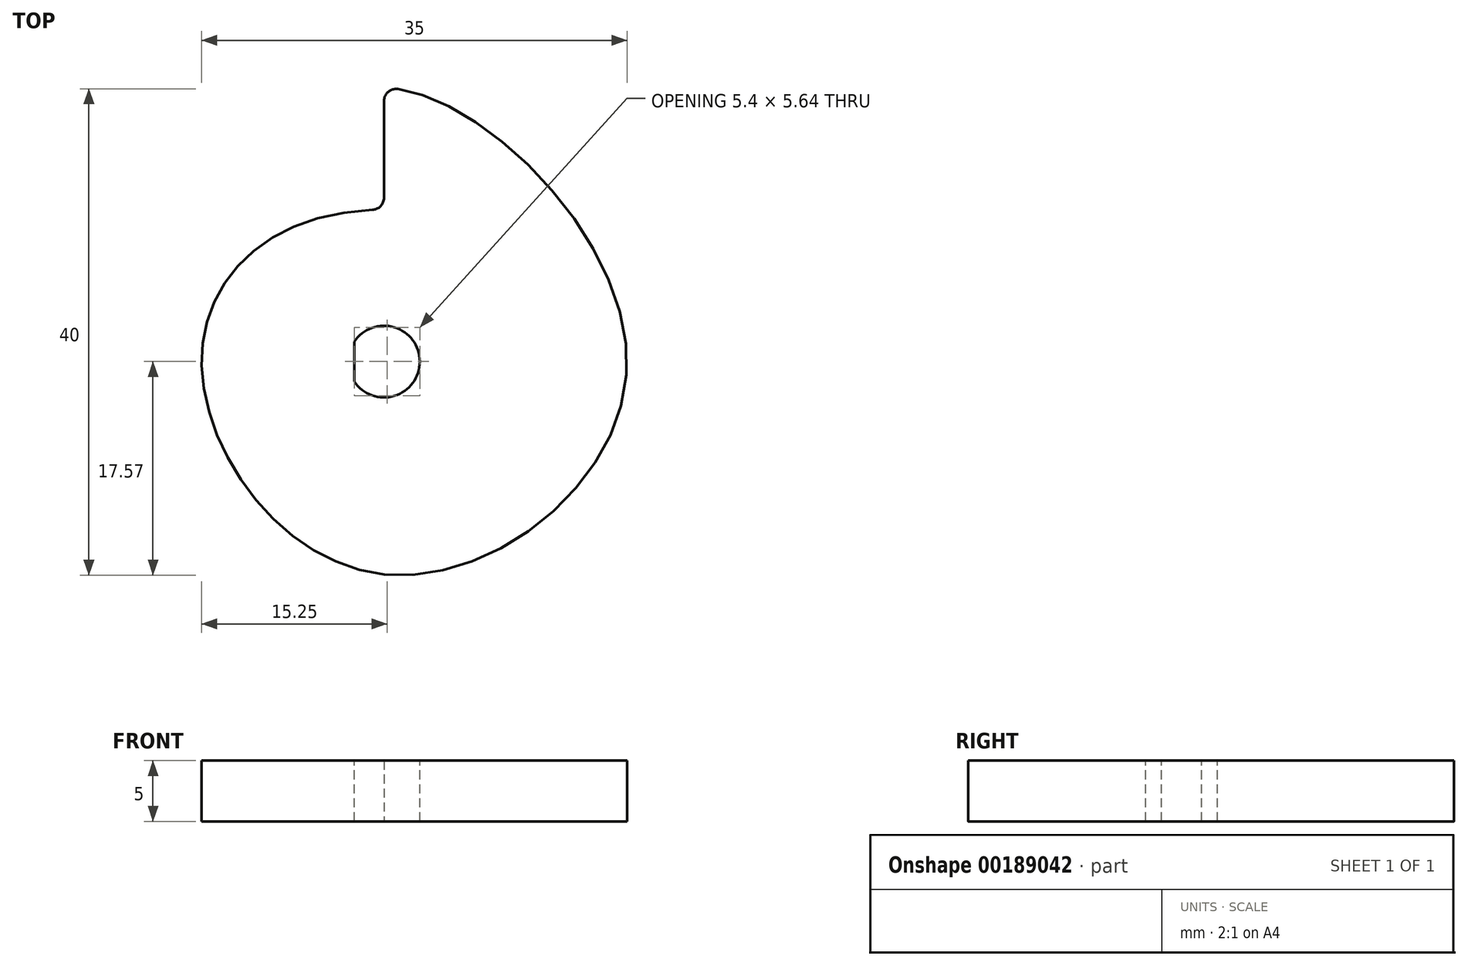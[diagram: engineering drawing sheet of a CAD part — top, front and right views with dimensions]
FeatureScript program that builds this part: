
annotation { "Feature Type Name" : "Feature", "Feature Type Description" : "" }
export const myFeature = defineFeature(function(context is Context, id is Id, definition is map)
    precondition{}
    {
        {
            var Q0;
            Q0=qCreatedBy(makeId("Top.planeOp"),FACE);
            var sketch = newSketch(context, id + "F0", { "sketchPlane" : qUnion([Q0])});
            skLineSegment(sketch, "E0", {"start": v(0, 21.43) * mm, "end": v(0, 13.48) * mm});
            skCircle(sketch, "E1", {"center": v(0, 0) * mm, "radius": 22.5 * mm, "construction": true});
            skCircle(sketch, "E2", {"center": v(0, 0) * mm, "radius": 12.5 * mm, "construction": true});
            skLineSegment(sketch, "E3", {"start": v(0, -12.5) * mm, "end": v(0, -22.5) * mm});
            skLineSegment(sketch, "E4", {"start": v(-12.5, 0) * mm, "end": v(-15, 0) * mm, "construction": true});
            skLineSegment(sketch, "E5", {"start": v(-15, 0) * mm, "end": v(-17.5, 0) * mm, "construction": true});
            skLineSegment(sketch, "E6", {"start": v(-17.5, 0) * mm, "end": v(-22.5, 0) * mm, "construction": true});
            skLineSegment(sketch, "E7", {"start": v(-17.5, 0) * mm, "end": v(-17.5, 12.5) * mm, "construction": true});
            skLineSegment(sketch, "E8", {"start": v(-17.5, 12.5) * mm, "end": v(-12.5, 12.5) * mm, "construction": true});
            skLineSegment(sketch, "E9", {"start": v(-12.5, 12.5) * mm, "end": v(-12.5, 0) * mm, "construction": true});
            skLineSegment(sketch, "E10", {"start": v(12.5, 0) * mm, "end": v(17.5, 0) * mm, "construction": true});
            skLineSegment(sketch, "E11", {"start": v(17.5, 0) * mm, "end": v(20, 0) * mm, "construction": true});
            skLineSegment(sketch, "E12", {"start": v(20, 0) * mm, "end": v(22.5, 0) * mm, "construction": true});
            skLineSegment(sketch, "E13", {"start": v(22.5, 0) * mm, "end": v(22.5, -12.5) * mm, "construction": true});
            skLineSegment(sketch, "E14", {"start": v(22.5, -12.5) * mm, "end": v(17.5, -12.5) * mm, "construction": true});
            skLineSegment(sketch, "E15", {"start": v(17.5, -12.5) * mm, "end": v(17.5, 0) * mm, "construction": true});
            skFitSpline(sketch, "E16", {"points": [v(0, 12.5) * mm, v(-15, 0) * mm, v(0, -17.5) * mm, v(20, 0) * mm, v(0, 22.5) * mm], "startDerivative": vector(-126.58, 0) * mm, "endDerivative": vector(-81.78, 0) * mm});
            skLineSegment(sketch, "E17", {"start": v(-15, 0) * mm, "end": v(-15, 12.5) * mm, "construction": true});
            skLineSegment(sketch, "E18", {"start": v(20, 0) * mm, "end": v(20, -12.5) * mm, "construction": true});
            skLineSegment(sketch, "E19", {"start": v(0, -22.5) * mm, "end": v(-8.7, -22.5) * mm, "construction": true});
            skLineSegment(sketch, "E20", {"start": v(-8.7, -22.5) * mm, "end": v(-8.7, -17.5) * mm, "construction": true});
            skLineSegment(sketch, "E21", {"start": v(-8.7, -17.5) * mm, "end": v(0, -17.5) * mm, "construction": true});
            skArc(sketch, "E22.filletArc", {"start": v(1.14, 22.41) * mm, "mid": v(0.35, 22.18) * mm, "end": v(0, 21.43) * mm});
            skArc(sketch, "E23.filletArc", {"start": v(-0.96, 12.48) * mm, "mid": v(-0.28, 12.79) * mm, "end": v(0, 13.48) * mm});
            skSolve(sketch);
        }
        {
            var Q0;
            Q0 = qSketchRegion(id + "F0", true);
            extrude(context, id + "F1", {"entities" : qUnion([Q0]), "depth" : 5 * mm});
        }
        {
            var Q0;
            Q0=makeQuery(id+"F1.opExtrude","CAP_FACE",FACE,{"disambiguationData":[OSD([sQuery(id+"F0.wireOp",EDGE,"E0"),sQuery(id+"F0.wireOp",EDGE,"E16")])],"isStart":false});
            var sketch = newSketch(context, id + "F2", { "sketchPlane" : qUnion([Q0])});
            skArc(sketch, "E24", {"start": v(-2.45, 1.64) * mm, "mid": v(2.95, 0) * mm, "end": v(-2.45, -1.64) * mm});
            skLineSegment(sketch, "E25", {"start": v(-2.45, -1.64) * mm, "end": v(-2.45, 1.64) * mm});
            skSolve(sketch);
        }
        {
            var Q0;
            Q0 = qSketchRegion(id + "F2", true);
            extrude(context, id + "F3", {"entities" : qUnion([Q0]), "operationType" : NewBodyOperationType.REMOVE, "oppositeDirection" : true, "depth" : 5 * mm});
        }
    });
